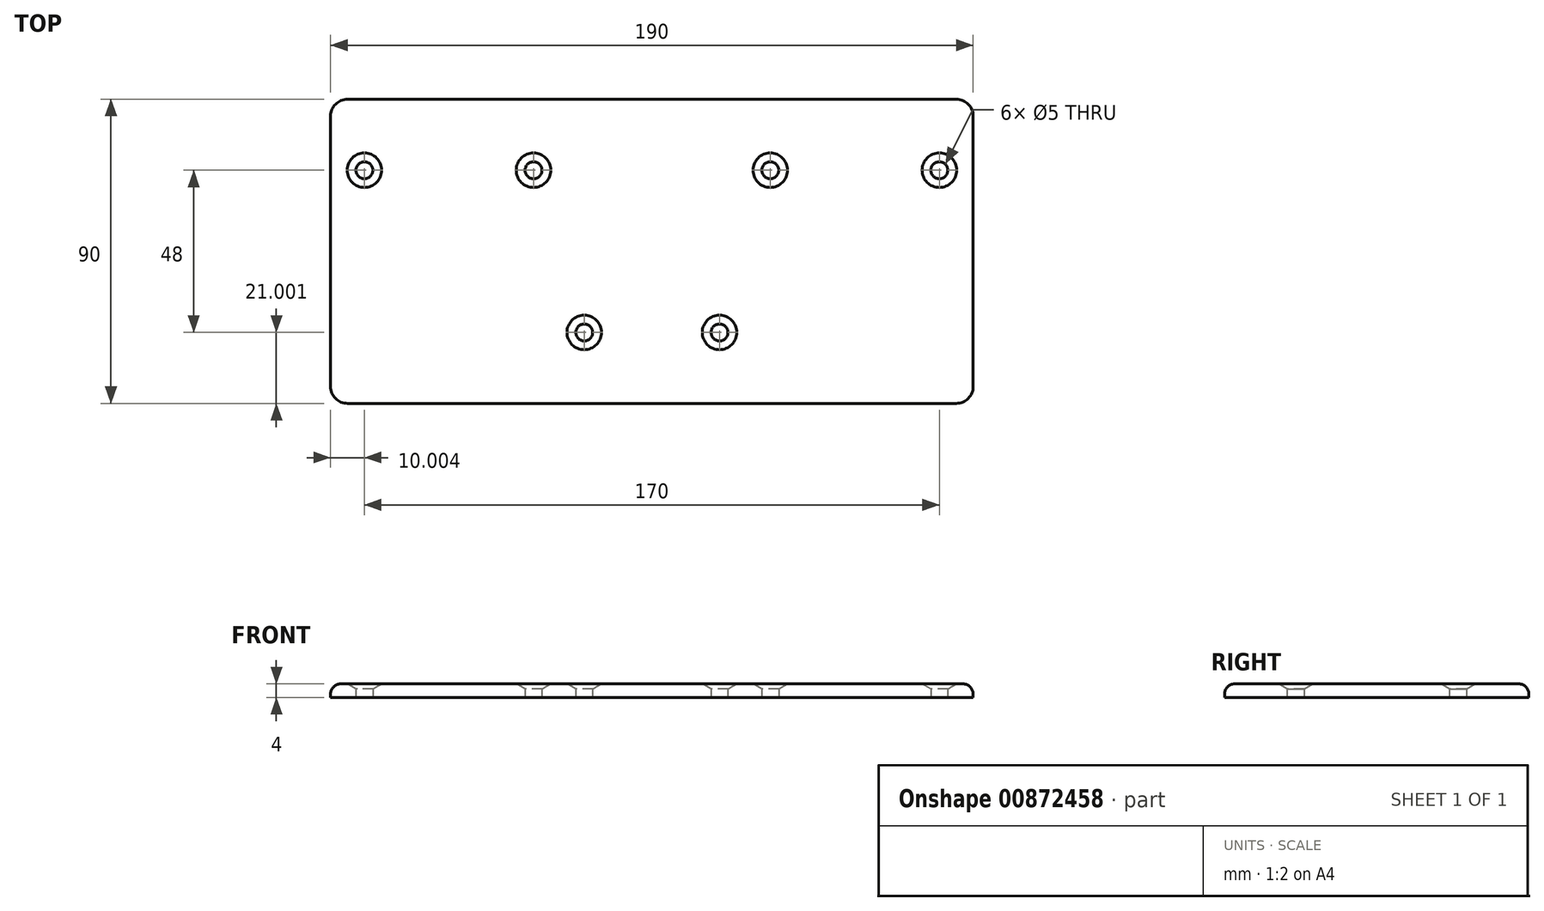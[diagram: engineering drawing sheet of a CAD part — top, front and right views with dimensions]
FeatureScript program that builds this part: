
annotation { "Feature Type Name" : "Feature", "Feature Type Description" : "" }
export const myFeature = defineFeature(function(context is Context, id is Id, definition is map)
    precondition{}
    {
        {
            var Q0;
            Q0=qCreatedBy(makeId("Top.planeOp"),FACE);
            var sketch = newSketch(context, id + "F0", { "sketchPlane" : qUnion([Q0])});
            skLineSegment(sketch, "E0.bottom", {"start": v(-105.94, 40.07) * mm, "end": v(84.06, 40.07) * mm});
            skLineSegment(sketch, "E0.top", {"start": v(-105.94, -49.93) * mm, "end": v(84.06, -49.93) * mm});
            skLineSegment(sketch, "E0.left", {"start": v(-105.94, 40.07) * mm, "end": v(-105.94, -49.93) * mm});
            skLineSegment(sketch, "E0.right", {"start": v(84.06, 40.07) * mm, "end": v(84.06, -49.93) * mm});
            skLineSegment(sketch, "E1", {"start": v(-105.94, 19.07) * mm, "end": v(84.06, 19.07) * mm});
            skLineSegment(sketch, "E2", {"start": v(-105.94, -28.93) * mm, "end": v(84.06, -28.93) * mm});
            skCircle(sketch, "E3", {"center": v(-95.94, 19.07) * mm, "radius": 2.5 * mm});
            skCircle(sketch, "E4", {"center": v(-45.94, 19.07) * mm, "radius": 2.5 * mm});
            skCircle(sketch, "E5", {"center": v(24.06, 19.07) * mm, "radius": 2.5 * mm});
            skCircle(sketch, "E6", {"center": v(74.06, 19.07) * mm, "radius": 2.5 * mm});
            skCircle(sketch, "E7", {"center": v(-30.94, -28.93) * mm, "radius": 2.5 * mm});
            skCircle(sketch, "E8", {"center": v(9.06, -28.93) * mm, "radius": 2.5 * mm});
            skSolve(sketch);
        }
        {
            var Q0;
            {var subQ12=sQuery(id+"F0.wireOp",EDGE,"E0.bottom");Q0=makeQuery(id+"F0.imprint","IMPRINT",FACE,{"disambiguationData":[TD([[makeQuery(id+"F0.imprint","IMPRINT",EDGE,{"derivedFrom":subQ12}),-1.0]])]});}
            var Q1;
            {var subQ0=sQuery(id+"F0.wireOp",EDGE,"E1");var subQ11=sQuery(id+"F0.wireOp",EDGE,"E0.left");var subQ12=makeQuery(id+"F0.imprint","INTERSECT",VERTEX,{"derivedFrom":[subQ11,subQ0]});Q1=makeQuery(id+"F0.imprint","IMPRINT",FACE,{"disambiguationData":[TD([[makeQuery(id+"F0.imprint","IMPRINT",EDGE,{"disambiguationData":[TD([[subQ12,-1.0]])],"derivedFrom":subQ11}),1.0]])]});}
            var Q2;
            {var subQ6=sQuery(id+"F0.wireOp",EDGE,"E0.top");Q2=makeQuery(id+"F0.imprint","IMPRINT",FACE,{"disambiguationData":[TD([[makeQuery(id+"F0.imprint","IMPRINT",EDGE,{"derivedFrom":subQ6}),1.0]])]});}
            extrude(context, id + "F1", {"entities" : qUnion([Q0, Q1, Q2]), "depth" : 4 * mm, "offsetDistance" : 25 * mm});
        }
        {
            var Q0;
            Q0=makeQuery(id+"F1.opExtrude","SWEPT_EDGE",EDGE,{"disambiguationData":[OSD([sQuery(id+"F0.wireOp",EDGE,"E0.bottom"),sQuery(id+"F0.wireOp",EDGE,"E0.left")])]});
            fillet(context, id + "F2", {"entities" : qUnion([Q0]), "radius" : 5 * mm, "tangentPropagation" : true, "allowEdgeOverflow" : false});
        }
        {
            var Q0;
            Q0=makeQuery(id+"F1.opExtrude","SWEPT_EDGE",EDGE,{"disambiguationData":[OSD([sQuery(id+"F0.wireOp",EDGE,"E0.bottom"),sQuery(id+"F0.wireOp",EDGE,"E0.right")])]});
            fillet(context, id + "F3", {"entities" : qUnion([Q0]), "radius" : 5 * mm, "tangentPropagation" : true, "allowEdgeOverflow" : false});
        }
        {
            var Q0;
            Q0=makeQuery(id+"F1.opExtrude","SWEPT_EDGE",EDGE,{"disambiguationData":[OSD([sQuery(id+"F0.wireOp",EDGE,"E0.top"),sQuery(id+"F0.wireOp",EDGE,"E0.right")])]});
            fillet(context, id + "F4", {"entities" : qUnion([Q0]), "radius" : 5 * mm, "tangentPropagation" : true, "allowEdgeOverflow" : false});
        }
        {
            var Q0;
            Q0=makeQuery(id+"F1.opExtrude","SWEPT_EDGE",EDGE,{"disambiguationData":[OSD([sQuery(id+"F0.wireOp",EDGE,"E0.top"),sQuery(id+"F0.wireOp",EDGE,"E0.left")])]});
            fillet(context, id + "F5", {"entities" : qUnion([Q0]), "radius" : 5 * mm, "tangentPropagation" : true, "allowEdgeOverflow" : false});
        }
        {
            var Q0;
            Q0=makeQuery(id+"F1.opExtrude","CAP_EDGE",EDGE,{"disambiguationData":[OSD([sQuery(id+"F0.wireOp",EDGE,"E0.top")])],"isStart":false});
            fillet(context, id + "F6", {"entities" : qUnion([Q0]), "radius" : 3 * mm, "tangentPropagation" : true, "allowEdgeOverflow" : false});
        }
        {
            var Q0;
            Q0=makeQuery(id+"F1.opExtrude","CAP_EDGE",EDGE,{"disambiguationData":[OSD([sQuery(id+"F0.wireOp",EDGE,"E3")])],"isStart":false});
            var Q1;
            Q1=makeQuery(id+"F1.opExtrude","CAP_EDGE",EDGE,{"disambiguationData":[OSD([sQuery(id+"F0.wireOp",EDGE,"E4")])],"isStart":false});
            var Q2;
            Q2=makeQuery(id+"F1.opExtrude","CAP_EDGE",EDGE,{"disambiguationData":[OSD([sQuery(id+"F0.wireOp",EDGE,"E5")])],"isStart":false});
            var Q3;
            Q3=makeQuery(id+"F1.opExtrude","CAP_EDGE",EDGE,{"disambiguationData":[OSD([sQuery(id+"F0.wireOp",EDGE,"E6")])],"isStart":false});
            var Q4;
            Q4=makeQuery(id+"F1.opExtrude","CAP_EDGE",EDGE,{"disambiguationData":[OSD([sQuery(id+"F0.wireOp",EDGE,"E8")])],"isStart":false});
            var Q5;
            Q5=makeQuery(id+"F1.opExtrude","CAP_EDGE",EDGE,{"disambiguationData":[OSD([sQuery(id+"F0.wireOp",EDGE,"E7")])],"isStart":false});
            chamfer(context, id + "F7", {"entities" : qUnion([Q0, Q1, Q2, Q3, Q4, Q5]), "chamferType" : ChamferType.OFFSET_ANGLE, "width" : 1.5 * mm, "oppositeDirection" : false, "angle" : 60 * degree, "tangentPropagation" : true});
        }
    });
